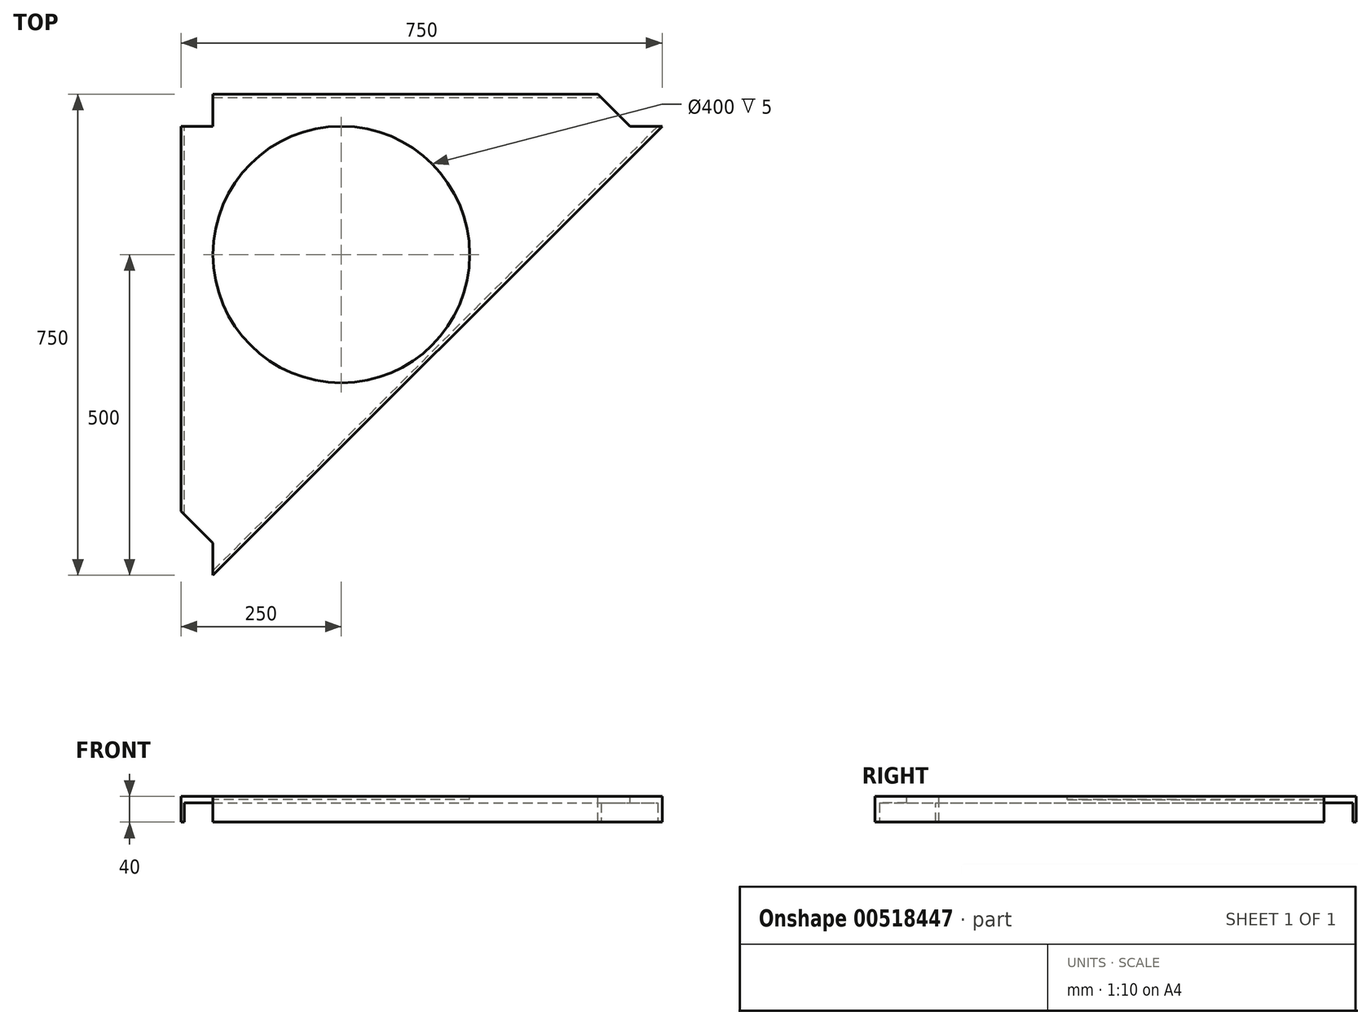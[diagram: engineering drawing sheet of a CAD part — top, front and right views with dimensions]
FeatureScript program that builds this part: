
annotation { "Feature Type Name" : "Feature", "Feature Type Description" : "" }
export const myFeature = defineFeature(function(context is Context, id is Id, definition is map)
    precondition{}
    {
        {
            var Q0;
            Q0=qCreatedBy(makeId("Top.planeOp"),FACE);
            var sketch = newSketch(context, id + "F0", { "sketchPlane" : qUnion([Q0])});
            skLineSegment(sketch, "E0", {"start": v(0, 0) * mm, "end": v(750, 0) * mm});
            skLineSegment(sketch, "E1", {"start": v(0, -750) * mm, "end": v(0, 0) * mm});
            skLineSegment(sketch, "E2", {"start": v(750, 0) * mm, "end": v(750, -50) * mm});
            skLineSegment(sketch, "E3", {"start": v(750, -50) * mm, "end": v(50, -750) * mm});
            skLineSegment(sketch, "E4", {"start": v(50, -750) * mm, "end": v(0, -750) * mm});
            skSolve(sketch);
        }
        {
            var Q0;
            Q0=makeQuery(id+"F0.imprint","IMPRINT",FACE,{"disambiguationData":[TD([[makeQuery(id+"F0.imprint","IMPRINT",EDGE,{"derivedFrom":sQuery(id+"F0.wireOp",EDGE,"E0")}),-1.0]])]});
            extrude(context, id + "F1", {"entities" : qUnion([Q0]), "depth" : 10 * mm, "offsetDistance" : 25 * mm});
        }
        {
            var Q0;
            Q0=makeQuery(id+"F1.opExtrude","SWEPT_EDGE",EDGE,{"disambiguationData":[OSD([sQuery(id+"F0.wireOp",EDGE,"E1"),sQuery(id+"F0.wireOp",EDGE,"E4")])]});
            var Q1;
            Q1=makeQuery(id+"F1.opExtrude","SWEPT_EDGE",EDGE,{"disambiguationData":[OSD([sQuery(id+"F0.wireOp",EDGE,"E0"),sQuery(id+"F0.wireOp",EDGE,"E2")])]});
            var Q2;
            Q2=makeQuery(id+"F1.opExtrude","SWEPT_EDGE",EDGE,{"disambiguationData":[OSD([sQuery(id+"F0.wireOp",EDGE,"E0"),sQuery(id+"F0.wireOp",EDGE,"E1")])]});
            fillet(context, id + "F2", {"entities" : qUnion([Q0, Q1, Q2]), "radius" : 5 * mm, "tangentPropagation" : true, "allowEdgeOverflow" : false});
        }
        {
            var Q0;
            Q0=makeQuery(id+"F1.opExtrude","CAP_FACE",FACE,{"disambiguationData":[OSD([sQuery(id+"F0.wireOp",EDGE,"E0"),sQuery(id+"F0.wireOp",EDGE,"E1"),sQuery(id+"F0.wireOp",EDGE,"PhSkESUb-ebmf-UgCL-A2DZ-lQ2So3ynJn3d"),sQuery(id+"F0.wireOp",EDGE,"E2"),sQuery(id+"F0.wireOp",EDGE,"E3"),sQuery(id+"F0.wireOp",EDGE,"E4")])],"isStart":false});
            var sketch = newSketch(context, id + "F3", { "sketchPlane" : qUnion([Q0])});
            skCircle(sketch, "E5", {"center": v(250, -250) * mm, "radius": 200 * mm});
            skSolve(sketch);
        }
        {
            var Q0;
            Q0=qSketchRegion(id+"F3",true);
            extrude(context, id + "F4", {"entities" : qUnion([Q0]), "operationType" : NewBodyOperationType.REMOVE, "oppositeDirection" : true, "depth" : 5 * mm, "offsetDistance" : 25 * mm});
        }
        {
            var Q0;
            Q0=makeQuery(id+"F1.opExtrude","CAP_FACE",FACE,{"disambiguationData":[OSD([sQuery(id+"F0.wireOp",EDGE,"E0"),sQuery(id+"F0.wireOp",EDGE,"E1"),sQuery(id+"F0.wireOp",EDGE,"E2"),sQuery(id+"F0.wireOp",EDGE,"E3"),sQuery(id+"F0.wireOp",EDGE,"E4")])],"isStart":true});
            var sketch = newSketch(context, id + "F5", { "sketchPlane" : qUnion([Q0])});
            skLineSegment(sketch, "E6.bottom", {"start": v(0, 720) * mm, "end": v(5, 720) * mm});
            skLineSegment(sketch, "E6.top", {"start": v(0, 30) * mm, "end": v(5, 30) * mm});
            skLineSegment(sketch, "E6.left", {"start": v(0, 720) * mm, "end": v(0, 30) * mm});
            skLineSegment(sketch, "E6.right", {"start": v(5, 720) * mm, "end": v(5, 30) * mm});
            skLineSegment(sketch, "E7.bottom", {"start": v(30, 0) * mm, "end": v(720, 0) * mm});
            skLineSegment(sketch, "E7.top", {"start": v(30, 5) * mm, "end": v(720, 5) * mm});
            skLineSegment(sketch, "E7.left", {"start": v(30, 0) * mm, "end": v(30, 5) * mm});
            skLineSegment(sketch, "E7.right", {"start": v(720, 0) * mm, "end": v(720, 5) * mm});
            skLineSegment(sketch, "E8", {"start": v(50, 750) * mm, "end": v(46.46, 746.46) * mm});
            skLineSegment(sketch, "E9", {"start": v(46.46, 746.46) * mm, "end": v(746.46, 46.46) * mm});
            skLineSegment(sketch, "E10", {"start": v(746.46, 46.46) * mm, "end": v(750, 50) * mm});
            skLineSegment(sketch, "E11", {"start": v(750, 50) * mm, "end": v(50, 750) * mm});
            skSolve(sketch);
        }
        {
            var Q0;
            Q0 = qSketchRegion(id + "F5", true);
            extrude(context, id + "F6", {"entities" : qUnion([Q0]), "operationType" : NewBodyOperationType.ADD, "depth" : 30 * mm, "offsetDistance" : 25 * mm});
        }
        {
            var Q0;
            Q0=makeQuery(id+"F1.opExtrude","CAP_FACE",FACE,{"disambiguationData":[OSD([sQuery(id+"F0.wireOp",EDGE,"E0"),sQuery(id+"F0.wireOp",EDGE,"E1"),sQuery(id+"F0.wireOp",EDGE,"PhSkESUb-ebmf-UgCL-A2DZ-lQ2So3ynJn3d"),sQuery(id+"F0.wireOp",EDGE,"E2"),sQuery(id+"F0.wireOp",EDGE,"E3"),sQuery(id+"F0.wireOp",EDGE,"E4")])],"isStart":false});
            var sketch = newSketch(context, id + "F7", { "sketchPlane" : qUnion([Q0])});
            skLineSegment(sketch, "E12.bottom", {"start": v(0, 0) * mm, "end": v(50, 0) * mm});
            skLineSegment(sketch, "E12.top", {"start": v(0, -50) * mm, "end": v(50, -50) * mm});
            skLineSegment(sketch, "E12.left", {"start": v(0, 0) * mm, "end": v(0, -50) * mm});
            skLineSegment(sketch, "E12.right", {"start": v(50, 0) * mm, "end": v(50, -50) * mm});
            skLineSegment(sketch, "E13.bottom", {"start": v(750, 0) * mm, "end": v(700, 0) * mm});
            skLineSegment(sketch, "E13.top", {"start": v(750, -50) * mm, "end": v(700, -50) * mm});
            skLineSegment(sketch, "E13.left", {"start": v(750, 0) * mm, "end": v(750, -50) * mm});
            skLineSegment(sketch, "E13.right", {"start": v(700, 0) * mm, "end": v(700, -50) * mm});
            skLineSegment(sketch, "E14.bottom", {"start": v(0, -750) * mm, "end": v(50, -750) * mm});
            skLineSegment(sketch, "E14.top", {"start": v(0, -700) * mm, "end": v(50, -700) * mm});
            skLineSegment(sketch, "E14.left", {"start": v(0, -750) * mm, "end": v(0, -700) * mm});
            skLineSegment(sketch, "E14.right", {"start": v(50, -750) * mm, "end": v(50, -700) * mm});
            skSolve(sketch);
        }
        {
            var Q0;
            Q0 = qSketchRegion(id + "F7", true);
            extrude(context, id + "F8", {"entities" : qUnion([Q0]), "operationType" : NewBodyOperationType.REMOVE, "endBound" : BoundingType.UP_TO_NEXT, "oppositeDirection" : true, "depth" : 25 * mm, "offsetDistance" : 25 * mm});
        }
        {
            var Q0;
            Q0=makeQuery(id+"F1.opExtrude","CAP_FACE",FACE,{"disambiguationData":[OSD([sQuery(id+"F0.wireOp",EDGE,"E0"),sQuery(id+"F0.wireOp",EDGE,"E1"),sQuery(id+"F0.wireOp",EDGE,"PhSkESUb-ebmf-UgCL-A2DZ-lQ2So3ynJn3d"),sQuery(id+"F0.wireOp",EDGE,"E2"),sQuery(id+"F0.wireOp",EDGE,"E3"),sQuery(id+"F0.wireOp",EDGE,"E4")])],"isStart":false});
            var sketch = newSketch(context, id + "F9", { "sketchPlane" : qUnion([Q0])});
            skLineSegment(sketch, "E15", {"start": v(700, -50) * mm, "end": v(650, 0) * mm});
            skLineSegment(sketch, "E16", {"start": v(650, 0) * mm, "end": v(700, 0) * mm});
            skLineSegment(sketch, "E17", {"start": v(700, 0) * mm, "end": v(700, -50) * mm});
            skLineSegment(sketch, "E18", {"start": v(0, -700) * mm, "end": v(0, -650) * mm});
            skLineSegment(sketch, "E19", {"start": v(0, -650) * mm, "end": v(50, -700) * mm});
            skLineSegment(sketch, "E20", {"start": v(50, -700) * mm, "end": v(0, -700) * mm});
            skSolve(sketch);
        }
        {
            var Q0;
            Q0 = qSketchRegion(id + "F9", true);
            extrude(context, id + "F10", {"entities" : qUnion([Q0]), "operationType" : NewBodyOperationType.REMOVE, "endBound" : BoundingType.UP_TO_NEXT, "oppositeDirection" : true, "depth" : 25 * mm, "offsetDistance" : 25 * mm});
        }
    });
